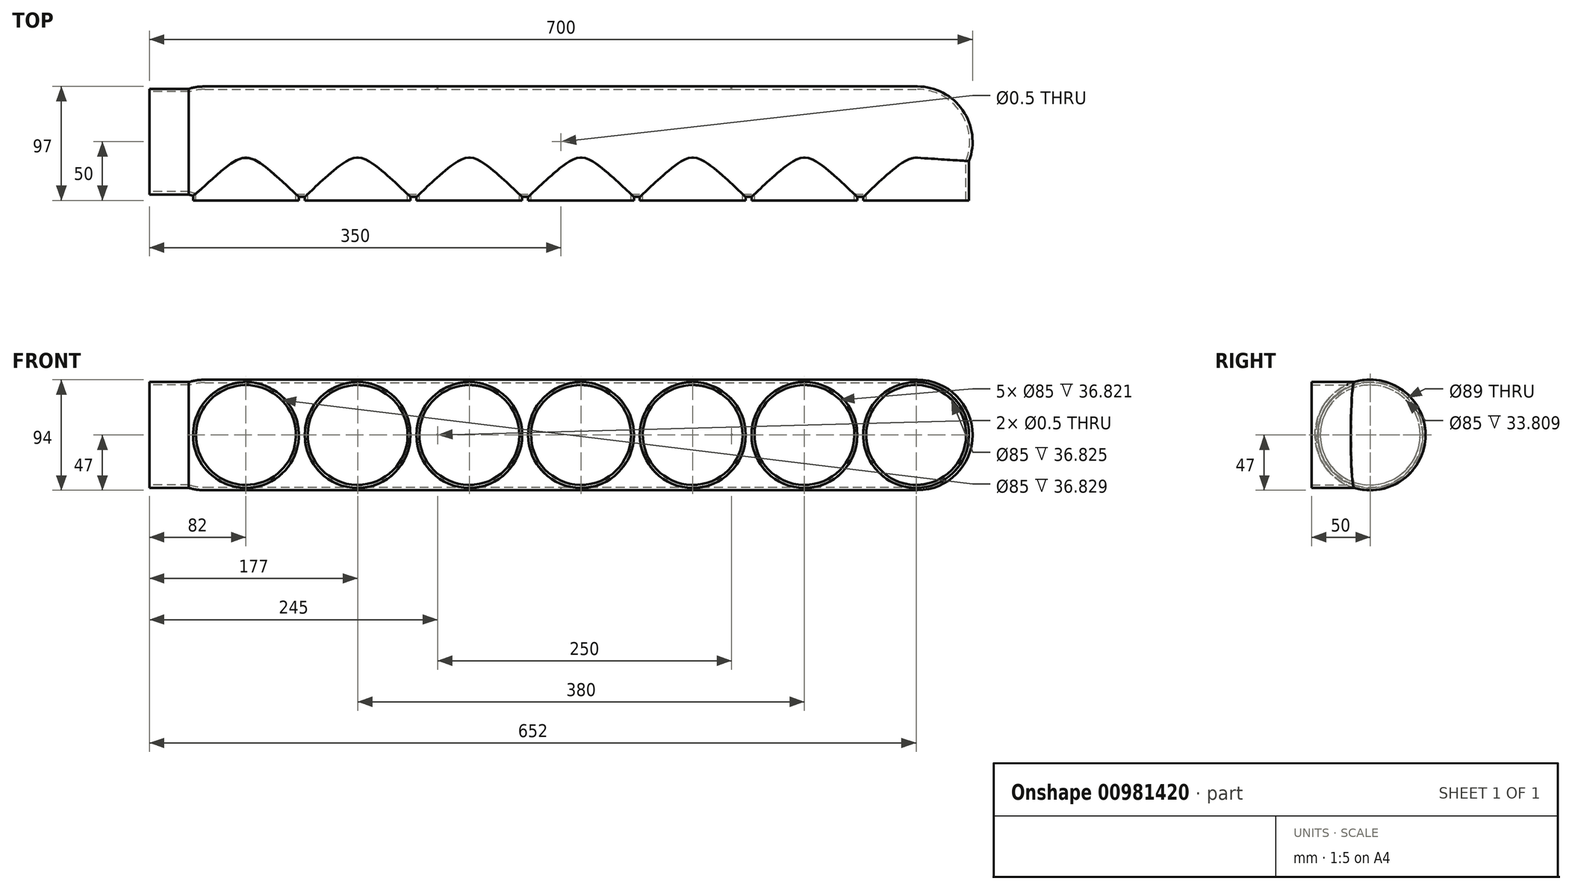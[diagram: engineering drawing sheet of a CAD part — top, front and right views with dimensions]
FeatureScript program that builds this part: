
annotation { "Feature Type Name" : "Feature", "Feature Type Description" : "" }
export const myFeature = defineFeature(function(context is Context, id is Id, definition is map)
    precondition{}
    {
        {
            var Q0;
            Q0=qCreatedBy(makeId("Front.planeOp"),FACE);
            var sketch = newSketch(context, id + "F0", { "sketchPlane" : qUnion([Q0])});
            skLineSegment(sketch, "E0.bottom", {"start": v(-350, 47) * mm, "end": v(350, 47) * mm});
            skLineSegment(sketch, "E0.top", {"start": v(-350, -47) * mm, "end": v(350, -47) * mm});
            skLineSegment(sketch, "E0.left", {"start": v(-350, 47) * mm, "end": v(-350, -47) * mm});
            skLineSegment(sketch, "E0.right", {"start": v(350, 47) * mm, "end": v(350, -47) * mm});
            skPoint(sketch, "E0.middle", {"position": v(0, 0) * mm});
            skSolve(sketch);
        }
        {
            var Q0;
            Q0=makeQuery(id+"F0.imprint","IMPRINT",FACE,{"disambiguationData":[TD([[makeQuery(id+"F0.imprint","IMPRINT",EDGE,{"derivedFrom":sQuery(id+"F0.wireOp",EDGE,"E0.bottom")}),-1.0]])]});
            extrude(context, id + "F1", {"entities" : qUnion([Q0]), "endBound" : BoundingType.SYMMETRIC, "depth" : 94 * mm, "offsetDistance" : 25 * mm});
        }
        {
            var Q0;
            Q0=makeQuery(id+"F1.opExtrude","SWEPT_FACE",FACE,{"disambiguationData":[OSD([sQuery(id+"F0.wireOp",EDGE,"E0.left")])]});
            cPlane(context, id + "F2", {"entities" : qUnion([Q0]), "cplaneType" : CPlaneType.OFFSET, "offset" : 0 * mm, "width" : 150 * mm, "height" : 150 * mm});
        }
        {
            var Q0;
            Q0=makeQuery(id+"F1.opExtrude","SWEPT_FACE",FACE,{"disambiguationData":[OSD([sQuery(id+"F0.wireOp",EDGE,"E0.bottom")])]});
            var Q1;
            Q1=makeQuery(id+"F1.opExtrude","CAP_FACE",FACE,{"disambiguationData":[OSD([sQuery(id+"F0.wireOp",EDGE,"E0.bottom"),sQuery(id+"F0.wireOp",EDGE,"E0.top"),sQuery(id+"F0.wireOp",EDGE,"E0.left"),sQuery(id+"F0.wireOp",EDGE,"E0.right")])],"isStart":false});
            var Q2;
            Q2=makeQuery(id+"F1.opExtrude","SWEPT_FACE",FACE,{"disambiguationData":[OSD([sQuery(id+"F0.wireOp",EDGE,"E0.top")])]});
            var Q3;
            Q3=makeQuery(id+"F1.opExtrude","CAP_FACE",FACE,{"disambiguationData":[OSD([sQuery(id+"F0.wireOp",EDGE,"E0.bottom"),sQuery(id+"F0.wireOp",EDGE,"E0.top"),sQuery(id+"F0.wireOp",EDGE,"E0.left"),sQuery(id+"F0.wireOp",EDGE,"E0.right")])],"isStart":true});
            var Q4;
            Q4=makeQuery(id+"F1.opExtrude","SWEPT_FACE",FACE,{"disambiguationData":[OSD([sQuery(id+"F0.wireOp",EDGE,"E0.right")])]});
            fillet(context, id + "F3", {"entities" : qUnion([Q0, Q1, Q2, Q3, Q4]), "radius" : 47 * mm, "tangentPropagation" : true, "allowEdgeOverflow" : false});
        }
        {
            var Q0;
            Q0=qCreatedBy(id+"F2.planeOp",FACE);
            var sketch = newSketch(context, id + "F4", { "sketchPlane" : qUnion([Q0])});
            skCircle(sketch, "E1", {"center": v(0, 0) * mm, "radius": 45 * mm});
            skSolve(sketch);
        }
        {
            var Q0;
            Q0 = qSketchRegion(id + "F4", true);
            extrude(context, id + "F5", {"entities" : qUnion([Q0]), "operationType" : NewBodyOperationType.ADD, "oppositeDirection" : true, "depth" : 100 * mm, "offsetDistance" : 25 * mm});
        }
        {
            var Q0;
            Q0=qCreatedBy(makeId("Front.planeOp"),FACE);
            var sketch = newSketch(context, id + "F6", { "sketchPlane" : qUnion([Q0])});
            skCircle(sketch, "E2", {"center": v(112, 0) * mm, "radius": 45 * mm});
            skCircle(sketch, "E3", {"center": v(207, 0) * mm, "radius": 45 * mm});
            skCircle(sketch, "E4", {"center": v(302, 0) * mm, "radius": 45 * mm});
            skCircle(sketch, "E5", {"center": v(-78, 0) * mm, "radius": 45 * mm});
            skCircle(sketch, "E6", {"center": v(-173, 0) * mm, "radius": 45 * mm});
            skCircle(sketch, "E7", {"center": v(-268, 0) * mm, "radius": 45 * mm});
            skCircle(sketch, "E8", {"center": v(17, 0) * mm, "radius": 45 * mm});
            skSolve(sketch);
        }
        {
            var Q0;
            Q0 = qSketchRegion(id + "F6", true);
            extrude(context, id + "F7", {"entities" : qUnion([Q0]), "operationType" : NewBodyOperationType.ADD, "depth" : 50 * mm, "offsetDistance" : 25 * mm});
        }
        {
            var Q0;
            Q0=makeQuery(id+"F7.opExtrude","CAP_FACE",FACE,{"disambiguationData":[OSD([sQuery(id+"F6.wireOp",EDGE,"E7")])],"isStart":false});
            var Q1;
            Q1=makeQuery(id+"F7.opExtrude","CAP_FACE",FACE,{"disambiguationData":[OSD([sQuery(id+"F6.wireOp",EDGE,"E6")])],"isStart":false});
            var Q2;
            Q2=makeQuery(id+"F7.opExtrude","CAP_FACE",FACE,{"disambiguationData":[OSD([sQuery(id+"F6.wireOp",EDGE,"E5")])],"isStart":false});
            var Q3;
            Q3=makeQuery(id+"F7.opExtrude","CAP_FACE",FACE,{"disambiguationData":[OSD([sQuery(id+"F6.wireOp",EDGE,"E8")])],"isStart":false});
            var Q4;
            Q4=makeQuery(id+"F7.opExtrude","CAP_FACE",FACE,{"disambiguationData":[OSD([sQuery(id+"F6.wireOp",EDGE,"E2")])],"isStart":false});
            var Q5;
            Q5=makeQuery(id+"F7.opExtrude","CAP_FACE",FACE,{"disambiguationData":[OSD([sQuery(id+"F6.wireOp",EDGE,"E3")])],"isStart":false});
            var Q6;
            Q6=makeQuery(id+"F7.opExtrude","CAP_FACE",FACE,{"disambiguationData":[OSD([sQuery(id+"F6.wireOp",EDGE,"E4")])],"isStart":false});
            var Q7;
            Q7=makeQuery(id+"F5.opExtrude","CAP_FACE",FACE,{"disambiguationData":[OSD([sQuery(id+"F4.wireOp",EDGE,"E1")])],"isStart":true});
            shell(context, id + "F8", {"entities" : qUnion([Q0, Q1, Q2, Q3, Q4, Q5, Q6, Q7]), "thickness" : 2.5 * mm});
        }
        {
            var Q0;
            Q0=qCreatedBy(makeId("Front.planeOp"),FACE);
            cPlane(context, id + "F9", {"entities" : qUnion([Q0]), "cplaneType" : CPlaneType.OFFSET, "offset" : 47 * mm, "oppositeDirection" : true, "width" : 150 * mm, "height" : 150 * mm});
        }
        {
            var Q0;
            Q0=qCreatedBy(id+"F9.planeOp",FACE);
            var sketch = newSketch(context, id + "F10", { "sketchPlane" : qUnion([Q0])});
            skPoint(sketch, "E9", {"position": v(145, 0) * mm});
            skPoint(sketch, "E10", {"position": v(-105, 0) * mm});
            skSolve(sketch);
        }
        {
            var Q0;
            Q0=sQuery(id+"F10.wireOp",VERTEX,"E9");
            var Q1;
            Q1=sQuery(id+"F10.wireOp",VERTEX,"E10");
            var Q2;
            Q2=makeQuery(id+"F1.opExtrude","SWEPT_BODY",BODY,{"disambiguationData":[OSD([sQuery(id+"F0.wireOp",EDGE,"E0.bottom"),sQuery(id+"F0.wireOp",EDGE,"E0.top"),sQuery(id+"F0.wireOp",EDGE,"E0.left"),sQuery(id+"F0.wireOp",EDGE,"E0.right")])]});
            hole(context, id + "F11", {"style" : HoleStyle.SIMPLE, "endStyle" : HoleEndStyle.BLIND, "oppositeDirection" : true, "holeDiameter" : 0.5 * mm, "majorDiameter" : 5 * mm, "holeDepth" : 50 * mm, "isTappedThrough" : true, "tappedDepth" : 12 * mm, "tapClearance" : 3, "startFromSketch" : true, "locations" : qUnion([Q0, Q1]), "scope" : qUnion([Q2])});
        }
        {
            var Q0;
            Q0=qCreatedBy(makeId("Top.planeOp"),FACE);
            var sketch = newSketch(context, id + "F12", { "sketchPlane" : qUnion([Q0])});
            skPoint(sketch, "E11", {"position": v(0, 0) * mm});
            skSolve(sketch);
        }
        {
            var Q0;
            Q0=sQuery(id+"F12.wireOp",VERTEX,"E11");
            var Q1;
            Q1=makeQuery(id+"F1.opExtrude","SWEPT_BODY",BODY,{"disambiguationData":[OSD([sQuery(id+"F0.wireOp",EDGE,"E0.bottom"),sQuery(id+"F0.wireOp",EDGE,"E0.top"),sQuery(id+"F0.wireOp",EDGE,"E0.left"),sQuery(id+"F0.wireOp",EDGE,"E0.right")])]});
            hole(context, id + "F13", {"style" : HoleStyle.SIMPLE, "endStyle" : HoleEndStyle.THROUGH, "holeDiameter" : 0.5 * mm, "majorDiameter" : 5 * mm, "isTappedThrough" : true, "tappedDepth" : 12 * mm, "tapClearance" : 3, "startFromSketch" : true, "locations" : qUnion([Q0]), "scope" : qUnion([Q1])});
        }
    });
